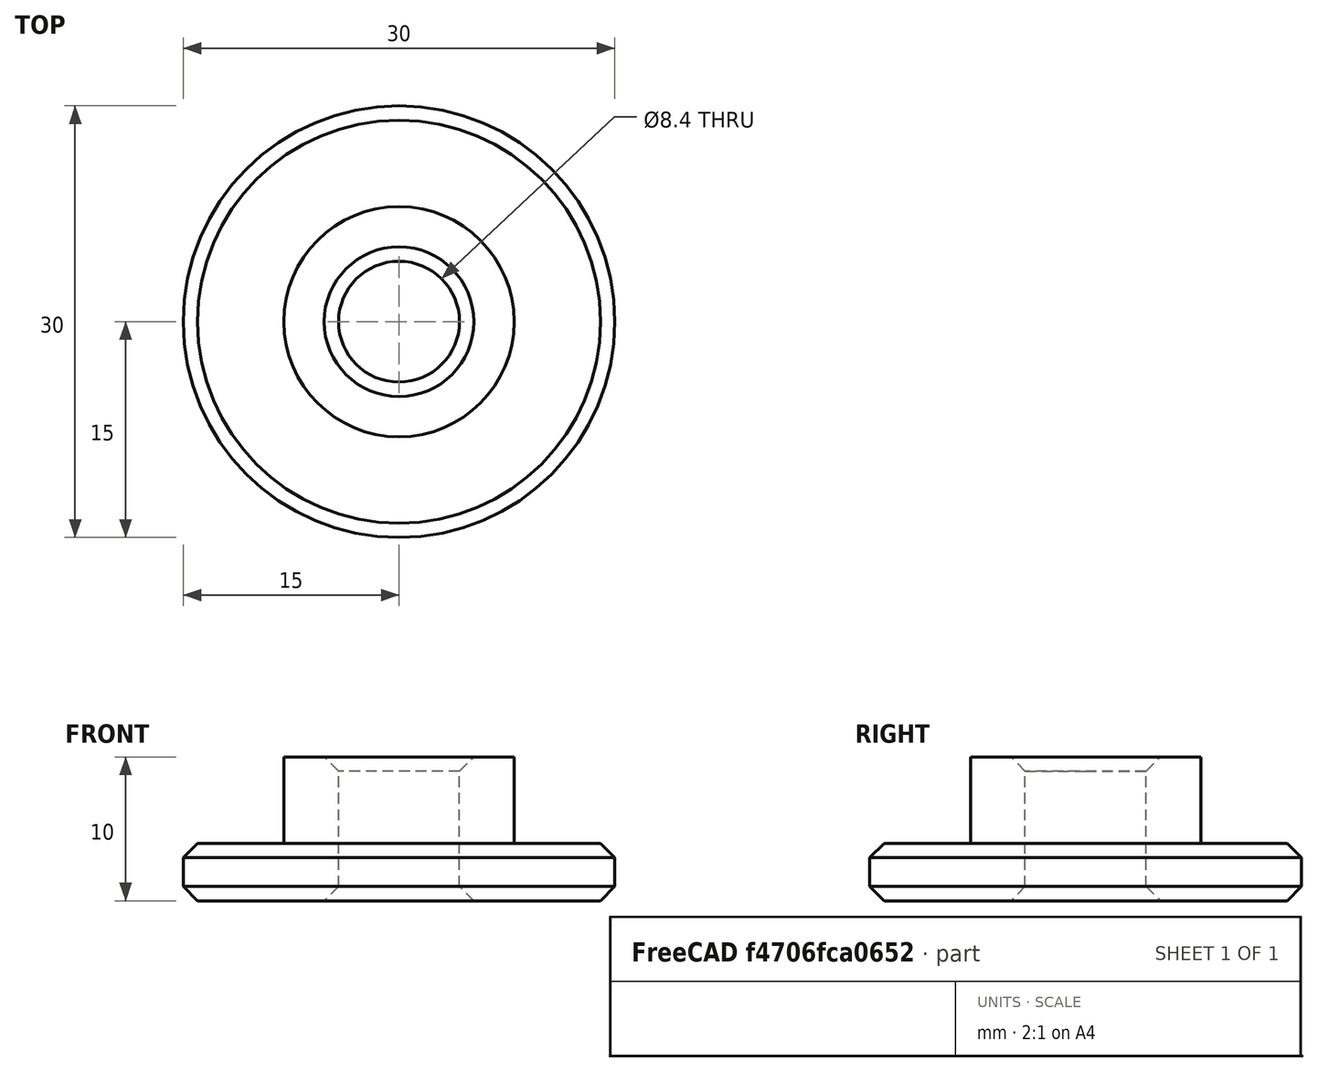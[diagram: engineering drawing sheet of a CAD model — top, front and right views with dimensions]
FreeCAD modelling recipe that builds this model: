
FCSTD DOCUMENT  (FreeCAD 0.18.4R)
Label: lawnmower-spacer-rear
License: All rights reserved
LicenseURL: http://en.wikipedia.org/wiki/All_rights_reserved
objects: PartDesign::AdditiveCylinder×2, PartDesign::Chamfer×2, PartDesign::SubtractiveCylinder×1, PartDesign::Body×1
note: 9 computed .brp shape members not serialized (recipe doc carries the construction recipe); baked Part::Feature solids carry a one-line shape summary decoded from their .brp

FEATURE [PartDesign::AdditiveCylinder] Cylinder
  Angle = 360
  AttacherType = Attacher::AttachEngine3D
  Height = 4
  Radius = 15
  Refine = true
FEATURE [PartDesign::AdditiveCylinder] Cylinder002
  Angle = 360
  AttacherType = Attacher::AttachEngine3D
  BaseFeature = -> Cylinder
  Height = 10
  Radius = 8
  Refine = true
FEATURE [PartDesign::SubtractiveCylinder] Cylinder003
  Angle = 360
  AttacherType = Attacher::AttachEngine3D
  BaseFeature = -> Cylinder002
  Height = 10
  Radius = 4.2
  Refine = true
FEATURE [PartDesign::Chamfer] Chamfer
  Base = -> Cylinder003 [Face1]
  BaseFeature = -> Cylinder003
  Size = 1
FEATURE [PartDesign::Chamfer] Chamfer001
  Base = -> Chamfer [Face6]
  BaseFeature = -> Chamfer
  Size = 1
FEATURE [PartDesign::Body] Body001
  Group = -> [Cylinder,Cylinder002,Cylinder003,Chamfer,Chamfer001]
  Origin = -> Origin001
  Tip = -> Chamfer001
